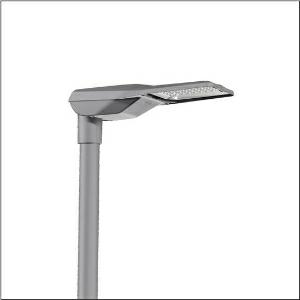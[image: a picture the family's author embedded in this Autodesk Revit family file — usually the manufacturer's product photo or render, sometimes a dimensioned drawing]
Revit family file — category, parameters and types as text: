
# Revit family: streetlight_sl_21_iq_mini___st0_8a_5xe2c31g08hb_2845
name_source: partatom
category: Lighting Fixtures
units: mm (PartAtom-declared; Revit-internal decimal feet)

## family parameters
Cut with Voids When Loaded = No
Host = Face
Light Source = No
Part Type = Normal
Room Calculation Point = No
Round Connector Dimension = Use Diameter
Shared = No

## types (1)
- --- (1 x LED, 9450 lm, 70.9 W, 3000K)
    Apparent Load = 71 VA
    CIE Flux Codes = 38 75 97 100 100
    Color Rendering = 70
    Color Temperature = 3000K
    Default Elevation = 1800 mm
    Description = Streetlight SL 21 mini, mast luminaire, primary light control with lens, of PMMA, primary optical cover: cover, of toughened safety glass, transparent, light distribution: ST0.8a, light emission: direct distribution, primary light characteristic: asymmetric, installation type: post-top, side-entry, LED, High Power LED, rated luminous flux: 9.450lm, luminous efficacy: 133lm/W, light colour: 730, colour temperature: 3000K, control gear: ECG iQ, control: Street-Remote, Auto-Match, Temp-Guard, Lumen-Switch, Night-Set, Smart-Wire, Light-Fading, Desk-Remote (wireless, voltage-free reading and setting of iQ features in the workshop via application-optimized NFC function/RFID function), optimised constant luminous flux control (CLO 2.0), mains connection: 220..240V, AC, 50/60Hz, start of lifetime: 71W, end of lifetime: 75W, reduction: 31W, luminaire housing, of diecast aluminium, powder-coated, Siteco® metallic grey (DB 702S), corrosivity category C5 according to DIN EN ISO 12944, length: 628mm, width: 235mm, height: 110mm, spigot size: 60/76mm (post-top) and 42/60/76mm (side-entry), mast flange for spigot size: 42mm: 5XC10008XM4, 60mm: 5XC10008XM2, 76/60mm: 5XC10108XM1, protection rating (complete): IP66, insulation class (complete): insulation class II (safety insulation), certification: CE, ENEC, VDE, impact resistance: IK09, permissible operating ambient temperature for outdoor applications: -40..+50°C, standard-compliant lighting for roads and squares, packaging unit: 1 piece

Light Distribution: ST0.8a
    Height = 110 mm
    Lamp = 1 x LED
    Lamp Light Flux = 9450 lm
    Lamp Power = 70.9 W
    Lamp count = 1
    Length = 625 mm
    Luminous efficacy = 133 lm/W
    Manufacturer = Siteco
    ModVariant = No
    Model = 5XE2C31G08HB
    Number of Poles = 1
    OnlyDefault = Yes
    Power Factor = 1
    Product Name = Streetlight SL 21 iQ mini | ST0.8a
    Product group = mast luminaire | pylon top
    ProductGroupID = 6100
    Protection Class = Protection class II
    Protection Degree = IP 66
    RLX_Detail_Level = 1
    RlxData = <blob elided: 93797 chars, md5=0750ae32>
    Socket = socket
    Standby Power = 0 W
    System Light Flux = 9450 lm
    System Power = 71 W
    Type Comments = factory setting: luminous flux: 100 % | dim-lin: 254 | 711 mA
    Type Image = l_1003519.jpg
    URL = http://relux.com
    VarID = @adj_068657
    Voltage = 0 V
    Weight = 0.00 kg
    Width = 234 mm

## geometry (parser evidence)
native form markers: Blend x4, Sweep x12
no freeform markers — native parametric forms only
